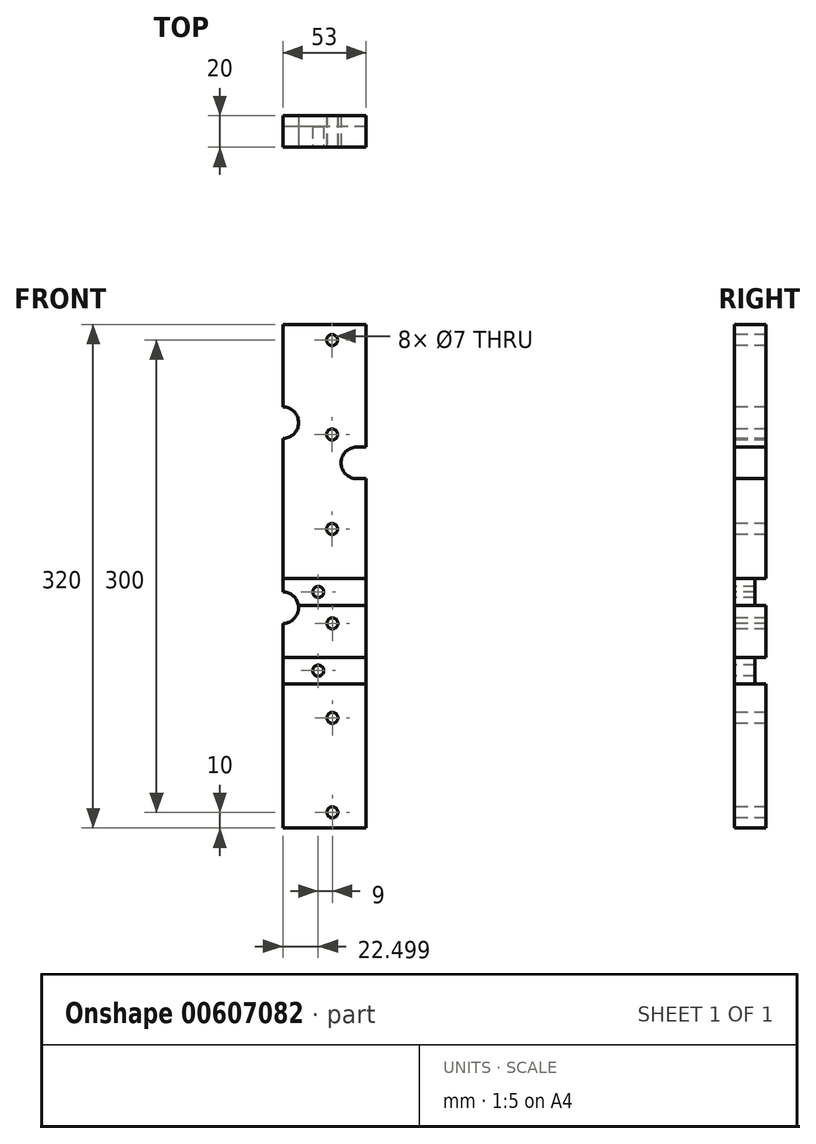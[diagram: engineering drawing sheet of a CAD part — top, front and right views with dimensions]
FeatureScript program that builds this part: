
annotation { "Feature Type Name" : "Feature", "Feature Type Description" : "" }
export const myFeature = defineFeature(function(context is Context, id is Id, definition is map)
    precondition{}
    {
        {
            var Q0;
            Q0=qCreatedBy(makeId("Front.planeOp"),FACE);
            var sketch = newSketch(context, id + "F0", { "sketchPlane" : qUnion([Q0])});
            skLineSegment(sketch, "E0.0", {"start": v(27.33, 104.58) * mm, "end": v(27.33, 157.08) * mm});
            skLineSegment(sketch, "E1.0", {"start": v(-25.67, 157.08) * mm, "end": v(27.33, 157.08) * mm});
            skLineSegment(sketch, "E2.0", {"start": v(-25.67, 79.08) * mm, "end": v(-25.67, 157.08) * mm});
            skArc(sketch, "E3.0", {"start": v(-19.67, 59.08) * mm, "mid": v(-9.67, 69.08) * mm, "end": v(-19.67, 79.08) * mm});
            skLineSegment(sketch, "E4.0", {"start": v(-25.67, 79.08) * mm, "end": v(-19.67, 79.08) * mm});
            skLineSegment(sketch, "E5.0", {"start": v(-25.67, 59.08) * mm, "end": v(-19.67, 59.08) * mm});
            skArc(sketch, "E6.0", {"start": v(27.33, 104.58) * mm, "mid": v(17.33, 94.58) * mm, "end": v(27.33, 84.58) * mm});
            skLineSegment(sketch, "E7.0", {"start": v(27.33, -12.92) * mm, "end": v(27.33, 84.58) * mm});
            skCircle(sketch, "E8.0", {"center": v(-3.97, 87.08) * mm, "radius": 3.5 * mm});
            skCircle(sketch, "E9.0", {"center": v(-3.97, 147.08) * mm, "radius": 3.5 * mm});
            skCircle(sketch, "E10.0", {"center": v(-3.97, 27.08) * mm, "radius": 3.5 * mm});
            skArc(sketch, "E11.0", {"start": v(27.33, -12.92) * mm, "mid": v(17.33, -22.92) * mm, "end": v(27.33, -32.92) * mm});
            skLineSegment(sketch, "E12.0", {"start": v(-25.67, -4.42) * mm, "end": v(27.33, -4.42) * mm});
            skCircle(sketch, "E13.0", {"center": v(4.83, -12.92) * mm, "radius": 3.5 * mm});
            skLineSegment(sketch, "E14.0", {"start": v(-25.67, -21.42) * mm, "end": v(17.44, -21.42) * mm});
            skLineSegment(sketch, "E15.0", {"start": v(-25.67, -162.92) * mm, "end": v(-25.67, 59.08) * mm});
            skCircle(sketch, "E16.0", {"center": v(-4.17, -32.92) * mm, "radius": 3.5 * mm});
            skCircle(sketch, "E17.0", {"center": v(4.83, -62.92) * mm, "radius": 3.5 * mm});
            skLineSegment(sketch, "E18.0", {"start": v(27.33, -162.92) * mm, "end": v(27.33, -32.92) * mm});
            skLineSegment(sketch, "E19.0", {"start": v(-25.67, -54.42) * mm, "end": v(27.33, -54.42) * mm});
            skLineSegment(sketch, "E20.0", {"start": v(-25.67, -71.42) * mm, "end": v(27.33, -71.42) * mm});
            skCircle(sketch, "E21.0", {"center": v(-4.17, -92.92) * mm, "radius": 3.5 * mm});
            skCircle(sketch, "E22.0", {"center": v(-4.17, -152.92) * mm, "radius": 3.5 * mm});
            skPoint(sketch, "E23.0", {"position": v(0.83, -162.92) * mm});
            skLineSegment(sketch, "E24.0", {"start": v(-25.67, -162.92) * mm, "end": v(27.33, -162.92) * mm});
            skLineSegment(sketch, "E25.MirrorCS", {"start": v(-25.67, 157.08) * mm, "end": v(-78.67, 157.08) * mm});
            skLineSegment(sketch, "E26.MirrorCS", {"start": v(-78.67, 104.58) * mm, "end": v(-78.67, 157.08) * mm});
            skArc(sketch, "E27.MirrorCS", {"start": v(-78.67, 104.58) * mm, "mid": v(-68.67, 94.58) * mm, "end": v(-78.67, 84.58) * mm});
            skLineSegment(sketch, "E28.MirrorCS", {"start": v(-78.67, -12.92) * mm, "end": v(-78.67, 84.58) * mm});
            skArc(sketch, "E29.MirrorCS", {"start": v(-31.67, 59.08) * mm, "mid": v(-41.67, 69.08) * mm, "end": v(-31.67, 79.08) * mm});
            skLineSegment(sketch, "E30.MirrorCS", {"start": v(-25.67, 59.08) * mm, "end": v(-31.67, 59.08) * mm});
            skLineSegment(sketch, "E31.MirrorCS", {"start": v(-25.67, 79.08) * mm, "end": v(-31.67, 79.08) * mm});
            skLineSegment(sketch, "E32.MirrorCS", {"start": v(-25.67, -4.42) * mm, "end": v(-78.67, -4.42) * mm});
            skLineSegment(sketch, "E33.MirrorCS", {"start": v(-25.67, -21.42) * mm, "end": v(-68.78, -21.42) * mm});
            skArc(sketch, "E34.MirrorCS", {"start": v(-78.67, -12.92) * mm, "mid": v(-68.67, -22.92) * mm, "end": v(-78.67, -32.92) * mm});
            skLineSegment(sketch, "E35.MirrorCS", {"start": v(-78.67, -162.92) * mm, "end": v(-78.67, -32.92) * mm});
            skLineSegment(sketch, "E36.MirrorCS", {"start": v(-25.67, -162.92) * mm, "end": v(-78.67, -162.92) * mm});
            skLineSegment(sketch, "E37.MirrorCS", {"start": v(-25.67, -54.42) * mm, "end": v(-78.67, -54.42) * mm});
            skLineSegment(sketch, "E38.MirrorCS", {"start": v(-25.67, -71.42) * mm, "end": v(-78.67, -71.42) * mm});
            skCircle(sketch, "E39.MirrorC", {"center": v(-47.17, -92.92) * mm, "radius": 3.5 * mm});
            skCircle(sketch, "E40.MirrorC", {"center": v(-47.17, -152.92) * mm, "radius": 3.5 * mm});
            skCircle(sketch, "E41.MirrorC", {"center": v(-56.17, -62.92) * mm, "radius": 3.5 * mm});
            skCircle(sketch, "E42.MirrorC", {"center": v(-47.17, -32.92) * mm, "radius": 3.5 * mm});
            skCircle(sketch, "E43.MirrorC", {"center": v(-56.17, -12.92) * mm, "radius": 3.5 * mm});
            skCircle(sketch, "E44.MirrorC", {"center": v(-47.37, 27.08) * mm, "radius": 3.5 * mm});
            skCircle(sketch, "E45.MirrorC", {"center": v(-47.37, 87.08) * mm, "radius": 3.5 * mm});
            skCircle(sketch, "E46.MirrorC", {"center": v(-47.37, 147.08) * mm, "radius": 3.5 * mm});
            skSolve(sketch);
        }
        {
            var Q0;
            Q0=makeQuery(id+"F0.imprint","IMPRINT",FACE,{"disambiguationData":[TD([[makeQuery(id+"F0.imprint","IMPRINT",EDGE,{"derivedFrom":sQuery(id+"F0.wireOp",EDGE,"E2.0")}),1.0]])]});
            var Q1;
            {var subQ1=sQuery(id+"F0.wireOp",EDGE,"E33.MirrorCS");Q1=makeQuery(id+"F0.imprint","IMPRINT",FACE,{"disambiguationData":[TD([[makeQuery(id+"F0.imprint","IMPRINT",EDGE,{"derivedFrom":subQ1}),1.0]])]});}
            var Q2;
            {var subQ0=sQuery(id+"F0.wireOp",EDGE,"E36.MirrorCS");Q2=makeQuery(id+"F0.imprint","IMPRINT",FACE,{"disambiguationData":[TD([[makeQuery(id+"F0.imprint","IMPRINT",EDGE,{"derivedFrom":subQ0}),-1.0]])]});}
            extrude(context, id + "F1", {"entities" : qUnion([Q0, Q1, Q2]), "oppositeDirection" : true, "depth" : 20 * mm, "offsetDistance" : 25 * mm});
        }
        {
            var Q0;
            {var subQ4=sQuery(id+"F0.wireOp",EDGE,"E32.MirrorCS");Q0=makeQuery(id+"F0.imprint","IMPRINT",FACE,{"disambiguationData":[TD([[makeQuery(id+"F0.imprint","IMPRINT",EDGE,{"derivedFrom":subQ4}),1.0]])]});}
            var Q1;
            {var subQ1=sQuery(id+"F0.wireOp",EDGE,"E37.MirrorCS");Q1=makeQuery(id+"F0.imprint","IMPRINT",FACE,{"disambiguationData":[TD([[makeQuery(id+"F0.imprint","IMPRINT",EDGE,{"derivedFrom":subQ1}),1.0]])]});}
            extrude(context, id + "F2", {"entities" : qUnion([Q0, Q1]), "oppositeDirection" : true, "depth" : 13 * mm, "offsetDistance" : 25 * mm});
        }
    });
